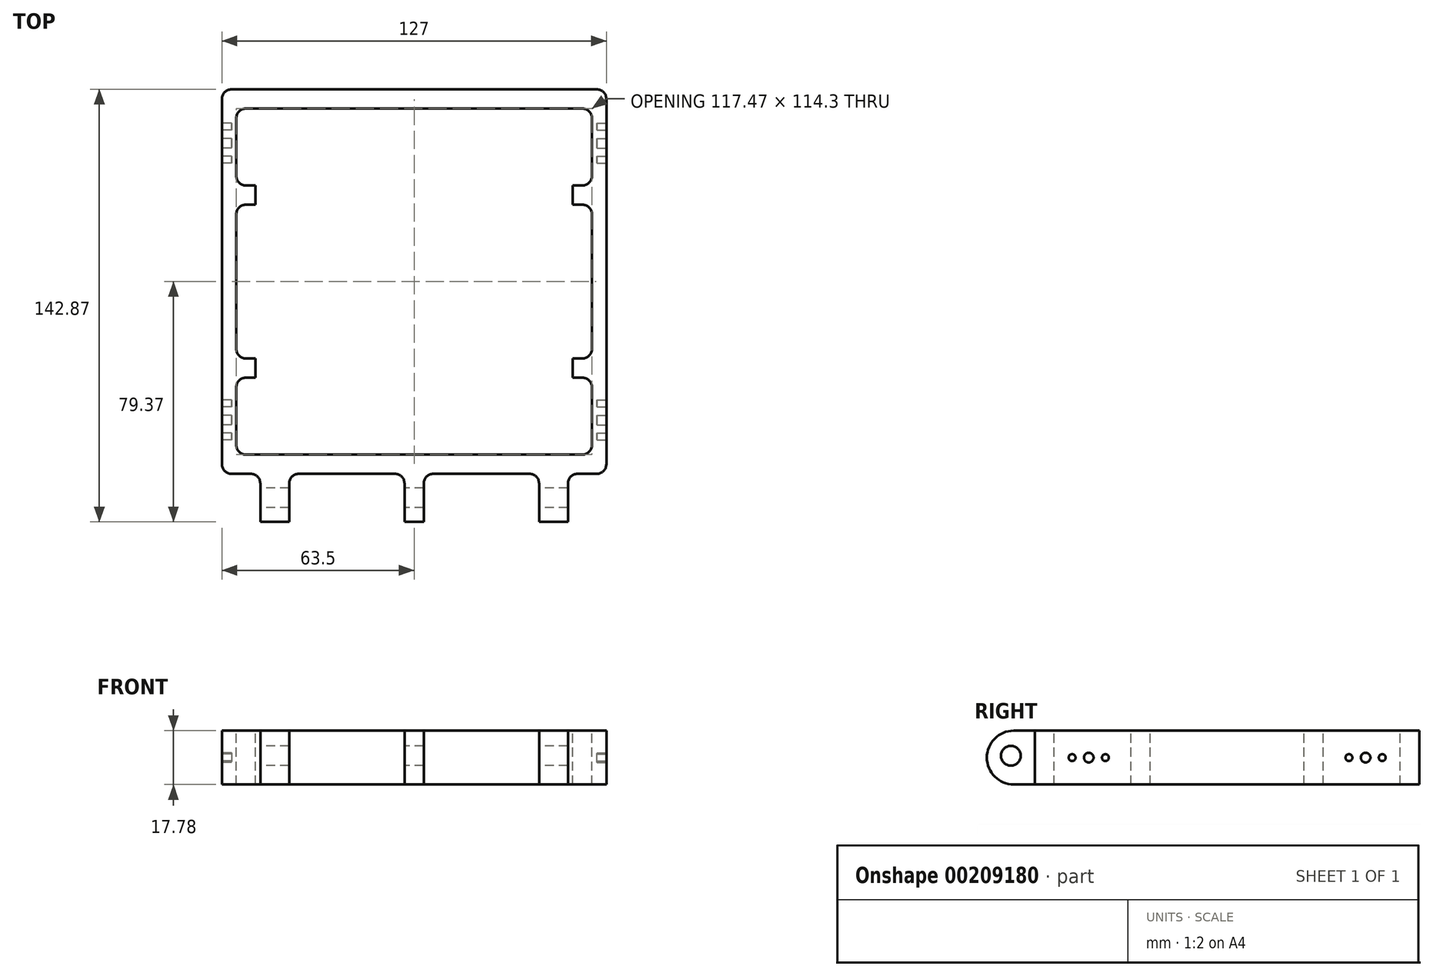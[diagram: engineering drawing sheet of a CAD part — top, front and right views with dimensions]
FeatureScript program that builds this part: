
annotation { "Feature Type Name" : "Feature", "Feature Type Description" : "" }
export const myFeature = defineFeature(function(context is Context, id is Id, definition is map)
    precondition{}
    {
        {
            var Q0;
            Q0=qCreatedBy(makeId("Top.planeOp"),FACE);
            var sketch = newSketch(context, id + "F0", { "sketchPlane" : qUnion([Q0])});
            skLineSegment(sketch, "E0.bottom", {"start": v(-63.5, 57.15) * mm, "end": v(63.5, 57.15) * mm});
            skLineSegment(sketch, "E0.top", {"start": v(-63.5, -69.85) * mm, "end": v(63.5, -69.85) * mm});
            skLineSegment(sketch, "E0.left", {"start": v(-63.5, 57.15) * mm, "end": v(-63.5, -69.85) * mm});
            skLineSegment(sketch, "E0.right", {"start": v(63.5, 57.15) * mm, "end": v(63.5, -69.85) * mm});
            skLineSegment(sketch, "E1.bottom", {"start": v(-50.8, -69.85) * mm, "end": v(-41.27, -69.85) * mm});
            skLineSegment(sketch, "E1.top", {"start": v(-50.8, -85.72) * mm, "end": v(-41.27, -85.72) * mm});
            skLineSegment(sketch, "E1.left", {"start": v(-50.8, -69.85) * mm, "end": v(-50.8, -85.72) * mm});
            skLineSegment(sketch, "E1.right", {"start": v(-41.27, -69.85) * mm, "end": v(-41.27, -85.72) * mm});
            skLineSegment(sketch, "E2.bottom", {"start": v(41.27, -69.85) * mm, "end": v(50.8, -69.85) * mm});
            skLineSegment(sketch, "E2.top", {"start": v(41.28, -85.72) * mm, "end": v(50.8, -85.72) * mm});
            skLineSegment(sketch, "E2.left", {"start": v(41.27, -69.85) * mm, "end": v(41.28, -85.72) * mm});
            skLineSegment(sketch, "E2.right", {"start": v(50.8, -69.85) * mm, "end": v(50.8, -85.72) * mm});
            skLineSegment(sketch, "E3.bottom", {"start": v(-3.17, -69.85) * mm, "end": v(3.18, -69.85) * mm});
            skLineSegment(sketch, "E3.top", {"start": v(-3.17, -85.72) * mm, "end": v(3.18, -85.72) * mm});
            skLineSegment(sketch, "E3.left", {"start": v(-3.17, -69.85) * mm, "end": v(-3.17, -85.72) * mm});
            skLineSegment(sketch, "E3.right", {"start": v(3.18, -69.85) * mm, "end": v(3.18, -85.72) * mm});
            skSolve(sketch);
        }
        {
            var Q0;
            Q0 = qSketchRegion(id + "F0", true);
            extrude(context, id + "F1", {"entities" : qUnion([Q0]), "depth" : 17.78 * mm});
        }
        {
            var Q0;
            Q0=makeQuery(id+"F1.opExtrude","CAP_FACE",FACE,{"disambiguationData":[OSD([sQuery(id+"F0.wireOp",EDGE,"E0.bottom"),sQuery(id+"F0.wireOp",EDGE,"E0.top"),sQuery(id+"F0.wireOp",EDGE,"E0.left"),sQuery(id+"F0.wireOp",EDGE,"E0.right")])],"isStart":false});
            var sketch = newSketch(context, id + "F2", { "sketchPlane" : qUnion([Q0])});
            skLineSegment(sketch, "E4.bottom", {"start": v(-58.74, 50.8) * mm, "end": v(3.17, 50.8) * mm});
            skLineSegment(sketch, "E4.top", {"start": v(-58.74, -63.5) * mm, "end": v(3.18, -63.5) * mm});
            skLineSegment(sketch, "E4.left", {"start": v(-58.74, 50.8) * mm, "end": v(-58.74, 25.4) * mm});
            skLineSegment(sketch, "E4.right", {"start": v(58.74, 50.8) * mm, "end": v(58.74, 25.4) * mm});
            skLineSegment(sketch, "E5.trimOffspring", {"start": v(3.17, 50.8) * mm, "end": v(58.74, 50.8) * mm});
            skLineSegment(sketch, "E6.trimOffspring", {"start": v(3.18, -63.5) * mm, "end": v(58.74, -63.5) * mm});
            skLineSegment(sketch, "E7.bottom", {"start": v(-58.74, 25.4) * mm, "end": v(-52.39, 25.4) * mm});
            skLineSegment(sketch, "E7.top", {"start": v(-58.74, 19.05) * mm, "end": v(-52.39, 19.05) * mm});
            skLineSegment(sketch, "E7.right", {"start": v(-52.39, 25.4) * mm, "end": v(-52.39, 19.05) * mm});
            skLineSegment(sketch, "E8.bottom", {"start": v(-58.74, -31.75) * mm, "end": v(-52.39, -31.75) * mm});
            skLineSegment(sketch, "E8.top", {"start": v(-58.74, -38.1) * mm, "end": v(-52.39, -38.1) * mm});
            skLineSegment(sketch, "E8.right", {"start": v(-52.39, -31.75) * mm, "end": v(-52.39, -38.1) * mm});
            skPoint(sketch, "E9.firstSnap0", {"position": v(-55.56, 25.4) * mm});
            skLineSegment(sketch, "E9.bottom", {"start": v(58.74, 25.4) * mm, "end": v(52.39, 25.4) * mm});
            skLineSegment(sketch, "E9.top", {"start": v(58.74, 19.05) * mm, "end": v(52.39, 19.05) * mm});
            skLineSegment(sketch, "E9.right", {"start": v(52.39, 25.4) * mm, "end": v(52.39, 19.05) * mm});
            skLineSegment(sketch, "E10.bottom", {"start": v(58.74, -31.75) * mm, "end": v(52.39, -31.75) * mm});
            skLineSegment(sketch, "E10.top", {"start": v(58.74, -38.1) * mm, "end": v(52.39, -38.1) * mm});
            skLineSegment(sketch, "E10.right", {"start": v(52.39, -31.75) * mm, "end": v(52.39, -38.1) * mm});
            skLineSegment(sketch, "E11.trimOffspring", {"start": v(-58.74, 19.05) * mm, "end": v(-58.74, -31.75) * mm});
            skLineSegment(sketch, "E12.trimOffspring", {"start": v(58.74, 19.05) * mm, "end": v(58.74, -31.75) * mm});
            skLineSegment(sketch, "E13.trimOffspring", {"start": v(-58.74, -38.1) * mm, "end": v(-58.74, -63.5) * mm});
            skLineSegment(sketch, "E14.trimOffspring", {"start": v(58.74, -38.1) * mm, "end": v(58.74, -63.5) * mm});
            skSolve(sketch);
        }
        {
            var Q0;
            Q0 = qSketchRegion(id + "F2", true);
            extrude(context, id + "F3", {"entities" : qUnion([Q0]), "operationType" : NewBodyOperationType.REMOVE, "endBound" : BoundingType.THROUGH_ALL, "oppositeDirection" : true, "depth" : 17.46 * mm});
        }
        {
            var Q0;
            Q0=makeQuery(id+"F3.boolean.opBoolean","COPY",EDGE,{"derivedFrom":makeQuery(id+"F3.opExtrude","SWEPT_EDGE",EDGE,{"disambiguationData":[OSD([sQuery(id+"F2.wireOp",EDGE,"E4.top"),sQuery(id+"F2.wireOp",EDGE,"E4.left")])]})});
            var Q1;
            Q1=makeQuery(id+"F3.boolean.opBoolean","COPY",EDGE,{"derivedFrom":makeQuery(id+"F3.opExtrude","SWEPT_EDGE",EDGE,{"disambiguationData":[OSD([sQuery(id+"F2.wireOp",EDGE,"E4.bottom"),sQuery(id+"F2.wireOp",EDGE,"E4.left")])]})});
            var Q2;
            Q2=makeQuery(id+"F3.boolean.opBoolean","COPY",EDGE,{"derivedFrom":makeQuery(id+"F3.opExtrude","SWEPT_EDGE",EDGE,{"disambiguationData":[OSD([sQuery(id+"F2.wireOp",EDGE,"E4.top"),sQuery(id+"F2.wireOp",EDGE,"E4.right")])]})});
            var Q3;
            Q3=makeQuery(id+"F3.boolean.opBoolean","COPY",EDGE,{"derivedFrom":makeQuery(id+"F3.opExtrude","SWEPT_EDGE",EDGE,{"disambiguationData":[OSD([sQuery(id+"F2.wireOp",EDGE,"E4.bottom"),sQuery(id+"F2.wireOp",EDGE,"E4.right")])]})});
            fillet(context, id + "F4", {"entities" : qUnion([Q0, Q1, Q2, Q3]), "radius" : 3.17 * mm, "tangentPropagation" : true, "allowEdgeOverflow" : false});
        }
        {
            var Q0;
            Q0=makeQuery(id+"F1.opExtrude","SWEPT_EDGE",EDGE,{"disambiguationData":[OSD([sQuery(id+"F0.wireOp",EDGE,"E0.top"),sQuery(id+"F0.wireOp",EDGE,"E0.left")])]});
            var Q1;
            Q1=makeQuery(id+"F1.opExtrude","SWEPT_EDGE",EDGE,{"disambiguationData":[OSD([sQuery(id+"F0.wireOp",EDGE,"E0.bottom"),sQuery(id+"F0.wireOp",EDGE,"E0.left")])]});
            var Q2;
            Q2=makeQuery(id+"F1.opExtrude","SWEPT_EDGE",EDGE,{"disambiguationData":[OSD([sQuery(id+"F0.wireOp",EDGE,"E0.top"),sQuery(id+"F0.wireOp",EDGE,"E0.right")])]});
            var Q3;
            Q3=makeQuery(id+"F1.opExtrude","SWEPT_EDGE",EDGE,{"disambiguationData":[OSD([sQuery(id+"F0.wireOp",EDGE,"E0.bottom"),sQuery(id+"F0.wireOp",EDGE,"E0.right")])]});
            fillet(context, id + "F5", {"entities" : qUnion([Q0, Q1, Q2, Q3]), "radius" : 3.17 * mm, "tangentPropagation" : true, "allowEdgeOverflow" : false});
        }
        {
            var Q0;
            Q0=makeQuery(id+"F1.opExtrude","SWEPT_EDGE",EDGE,{"disambiguationData":[OSD([sQuery(id+"F0.wireOp",EDGE,"E0.top"),sQuery(id+"F0.wireOp",EDGE,"E1.bottom"),sQuery(id+"F0.wireOp",EDGE,"E1.right")])]});
            var Q1;
            Q1=makeQuery(id+"F1.opExtrude","SWEPT_EDGE",EDGE,{"disambiguationData":[OSD([sQuery(id+"F0.wireOp",EDGE,"E0.top"),sQuery(id+"F0.wireOp",EDGE,"E3.bottom"),sQuery(id+"F0.wireOp",EDGE,"E3.right")])]});
            var Q2;
            Q2=makeQuery(id+"F1.opExtrude","SWEPT_EDGE",EDGE,{"disambiguationData":[OSD([sQuery(id+"F0.wireOp",EDGE,"E0.top"),sQuery(id+"F0.wireOp",EDGE,"E2.bottom"),sQuery(id+"F0.wireOp",EDGE,"E2.right")])]});
            var Q3;
            Q3=makeQuery(id+"F1.opExtrude","SWEPT_EDGE",EDGE,{"disambiguationData":[OSD([sQuery(id+"F0.wireOp",EDGE,"E0.top"),sQuery(id+"F0.wireOp",EDGE,"E1.bottom"),sQuery(id+"F0.wireOp",EDGE,"E1.left")])]});
            var Q4;
            Q4=makeQuery(id+"F1.opExtrude","SWEPT_EDGE",EDGE,{"disambiguationData":[OSD([sQuery(id+"F0.wireOp",EDGE,"E0.top"),sQuery(id+"F0.wireOp",EDGE,"E3.bottom"),sQuery(id+"F0.wireOp",EDGE,"E3.left")])]});
            var Q5;
            Q5=makeQuery(id+"F1.opExtrude","SWEPT_EDGE",EDGE,{"disambiguationData":[OSD([sQuery(id+"F0.wireOp",EDGE,"E0.top"),sQuery(id+"F0.wireOp",EDGE,"E2.bottom"),sQuery(id+"F0.wireOp",EDGE,"E2.left")])]});
            fillet(context, id + "F6", {"entities" : qUnion([Q0, Q1, Q2, Q3, Q4, Q5]), "radius" : 3.17 * mm, "tangentPropagation" : true, "allowEdgeOverflow" : false});
        }
        {
            var Q0;
            Q0=makeQuery(id+"F1.opExtrude","SWEPT_FACE",FACE,{"disambiguationData":[OSD([sQuery(id+"F0.wireOp",EDGE,"E1.left")])]});
            var sketch = newSketch(context, id + "F7", { "sketchPlane" : qUnion([Q0])});
            skCircle(sketch, "E15", {"center": v(77.79, 9.53) * mm, "radius": 3.26 * mm});
            skSolve(sketch);
        }
        {
            var Q0;
            Q0 = qSketchRegion(id + "F7", true);
            extrude(context, id + "F8", {"entities" : qUnion([Q0]), "operationType" : NewBodyOperationType.REMOVE, "endBound" : BoundingType.THROUGH_ALL, "oppositeDirection" : true, "depth" : 25.4 * mm});
        }
        {
            var Q0;
            Q0=makeQuery(id+"F1.opExtrude","CAP_EDGE",EDGE,{"disambiguationData":[OSD([sQuery(id+"F0.wireOp",EDGE,"E1.top")])],"isStart":false});
            var Q1;
            Q1=makeQuery(id+"F1.opExtrude","CAP_EDGE",EDGE,{"disambiguationData":[OSD([sQuery(id+"F0.wireOp",EDGE,"E3.top")])],"isStart":false});
            var Q2;
            Q2=makeQuery(id+"F1.opExtrude","CAP_EDGE",EDGE,{"disambiguationData":[OSD([sQuery(id+"F0.wireOp",EDGE,"E2.top")])],"isStart":false});
            fillet(context, id + "F9", {"entities" : qUnion([Q0, Q1, Q2]), "radius" : 8.9 * mm, "tangentPropagation" : true, "allowEdgeOverflow" : false});
        }
        {
            var Q0;
            Q0=makeQuery(id+"F1.opExtrude","CAP_EDGE",EDGE,{"disambiguationData":[OSD([sQuery(id+"F0.wireOp",EDGE,"E1.top")])],"isStart":true});
            var Q1;
            Q1=makeQuery(id+"F1.opExtrude","CAP_EDGE",EDGE,{"disambiguationData":[OSD([sQuery(id+"F0.wireOp",EDGE,"E3.top")])],"isStart":true});
            var Q2;
            Q2=makeQuery(id+"F1.opExtrude","CAP_EDGE",EDGE,{"disambiguationData":[OSD([sQuery(id+"F0.wireOp",EDGE,"E2.top")])],"isStart":true});
            fillet(context, id + "F10", {"entities" : qUnion([Q0, Q1, Q2]), "radius" : 8.9 * mm, "tangentPropagation" : true, "allowEdgeOverflow" : false});
        }
        {
            var Q0;
            Q0=makeQuery(id+"F1.opExtrude","SWEPT_FACE",FACE,{"disambiguationData":[OSD([sQuery(id+"F0.wireOp",EDGE,"E0.right")])]});
            var sketch = newSketch(context, id + "F11", { "sketchPlane" : qUnion([Q0])});
            skCircle(sketch, "E16", {"center": v(-52.07, 8.9) * mm, "radius": 1.59 * mm});
            skCircle(sketch, "E17", {"center": v(-46.57, 8.9) * mm, "radius": 1.14 * mm});
            skCircle(sketch, "E18", {"center": v(39.37, 8.9) * mm, "radius": 1.59 * mm});
            skCircle(sketch, "E19", {"center": v(33.87, 8.9) * mm, "radius": 1.14 * mm});
            skCircle(sketch, "E20", {"center": v(-57.57, 8.9) * mm, "radius": 1.14 * mm});
            skCircle(sketch, "E21", {"center": v(44.87, 8.9) * mm, "radius": 1.14 * mm});
            skSolve(sketch);
        }
        {
            var Q0;
            Q0 = qSketchRegion(id + "F11", true);
            extrude(context, id + "F12", {"entities" : qUnion([Q0]), "operationType" : NewBodyOperationType.REMOVE, "oppositeDirection" : true, "depth" : 3.17 * mm});
        }
        {
            var Q0;
            Q0=makeQuery(id+"F3.boolean.opBoolean","COPY",EDGE,{"derivedFrom":makeQuery(id+"F3.opExtrude","SWEPT_EDGE",EDGE,{"disambiguationData":[OSD([sQuery(id+"F2.wireOp",EDGE,"E10.bottom"),sQuery(id+"F2.wireOp",EDGE,"E12.trimOffspring")])]})});
            var Q1;
            Q1=makeQuery(id+"F3.boolean.opBoolean","COPY",EDGE,{"derivedFrom":makeQuery(id+"F3.opExtrude","SWEPT_EDGE",EDGE,{"disambiguationData":[OSD([sQuery(id+"F2.wireOp",EDGE,"E10.top"),sQuery(id+"F2.wireOp",EDGE,"E14.trimOffspring")])]})});
            var Q2;
            Q2=makeQuery(id+"F3.boolean.opBoolean","COPY",EDGE,{"derivedFrom":makeQuery(id+"F3.opExtrude","SWEPT_EDGE",EDGE,{"disambiguationData":[OSD([sQuery(id+"F2.wireOp",EDGE,"E9.top"),sQuery(id+"F2.wireOp",EDGE,"E12.trimOffspring")])]})});
            var Q3;
            Q3=makeQuery(id+"F3.boolean.opBoolean","COPY",EDGE,{"derivedFrom":makeQuery(id+"F3.opExtrude","SWEPT_EDGE",EDGE,{"disambiguationData":[OSD([sQuery(id+"F2.wireOp",EDGE,"Q3D4xbYD-Hvlc-532o-LolA-R2ixiTeDqwoF.right"),sQuery(id+"F2.wireOp",EDGE,"E5.trimOffspring")])]})});
            var Q4;
            Q4=makeQuery(id+"F3.boolean.opBoolean","COPY",EDGE,{"derivedFrom":makeQuery(id+"F3.opExtrude","SWEPT_EDGE",EDGE,{"disambiguationData":[OSD([sQuery(id+"F2.wireOp",EDGE,"E7.top"),sQuery(id+"F2.wireOp",EDGE,"E11.trimOffspring")])]})});
            var Q5;
            Q5=makeQuery(id+"F3.boolean.opBoolean","COPY",EDGE,{"derivedFrom":makeQuery(id+"F3.opExtrude","SWEPT_EDGE",EDGE,{"disambiguationData":[OSD([sQuery(id+"F2.wireOp",EDGE,"0K5OecD9-GTQg-UlPH-IUjA-I7lC0x8ed1Ou.right"),sQuery(id+"F2.wireOp",EDGE,"E6.trimOffspring")])]})});
            var Q6;
            Q6=makeQuery(id+"F3.boolean.opBoolean","COPY",EDGE,{"derivedFrom":makeQuery(id+"F3.opExtrude","SWEPT_EDGE",EDGE,{"disambiguationData":[OSD([sQuery(id+"F2.wireOp",EDGE,"E8.top"),sQuery(id+"F2.wireOp",EDGE,"E13.trimOffspring")])]})});
            fillet(context, id + "F13", {"entities" : qUnion([Q0, Q1, Q2, Q3, Q4, Q5, Q6]), "radius" : 3.17 * mm, "tangentPropagation" : true, "allowEdgeOverflow" : false});
        }
        {
            var Q0;
            Q0=makeQuery(id+"F3.boolean.opBoolean","COPY",EDGE,{"derivedFrom":makeQuery(id+"F3.opExtrude","SWEPT_EDGE",EDGE,{"disambiguationData":[OSD([sQuery(id+"F2.wireOp",EDGE,"E8.bottom"),sQuery(id+"F2.wireOp",EDGE,"E11.trimOffspring")])]})});
            fillet(context, id + "F14", {"entities" : qUnion([Q0]), "radius" : 3.17 * mm, "tangentPropagation" : true, "allowEdgeOverflow" : false});
        }
        {
            var Q0;
            Q0=makeQuery(id+"F1.opExtrude","SWEPT_FACE",FACE,{"disambiguationData":[OSD([sQuery(id+"F0.wireOp",EDGE,"E0.left")])]});
            var sketch = newSketch(context, id + "F15", { "sketchPlane" : qUnion([Q0])});
            skCircle(sketch, "E22", {"center": v(-39.37, 8.9) * mm, "radius": 1.59 * mm});
            skCircle(sketch, "E23", {"center": v(-33.87, 8.89) * mm, "radius": 1.14 * mm});
            skCircle(sketch, "E24", {"center": v(-44.87, 8.9) * mm, "radius": 1.14 * mm});
            skCircle(sketch, "E25", {"center": v(52.07, 8.9) * mm, "radius": 1.59 * mm});
            skCircle(sketch, "E26", {"center": v(57.57, 8.9) * mm, "radius": 1.14 * mm});
            skCircle(sketch, "E27", {"center": v(46.57, 8.9) * mm, "radius": 1.14 * mm});
            skSolve(sketch);
        }
        {
            var Q0;
            Q0 = qSketchRegion(id + "F15", true);
            extrude(context, id + "F16", {"entities" : qUnion([Q0]), "operationType" : NewBodyOperationType.REMOVE, "oppositeDirection" : true, "depth" : 3.17 * mm});
        }
    });
